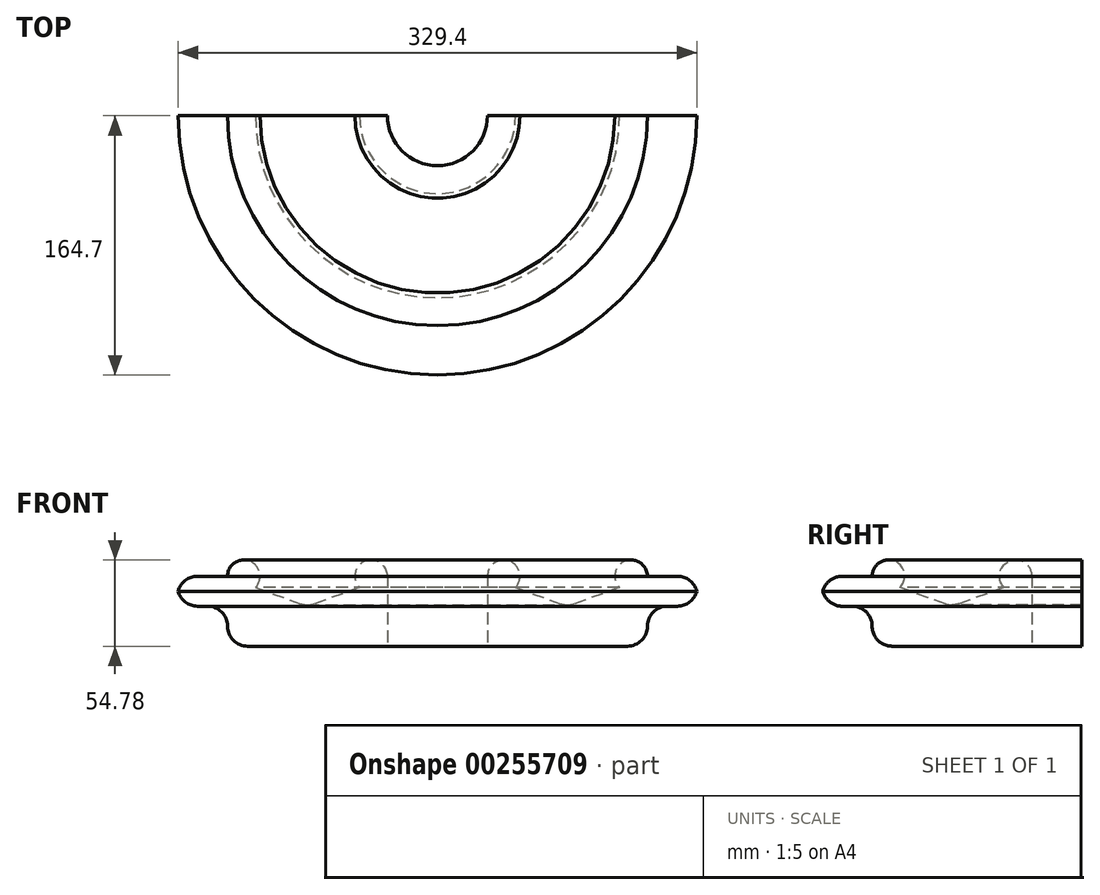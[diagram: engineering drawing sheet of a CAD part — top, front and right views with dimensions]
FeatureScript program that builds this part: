
annotation { "Feature Type Name" : "Feature", "Feature Type Description" : "" }
export const myFeature = defineFeature(function(context is Context, id is Id, definition is map)
    precondition{}
    {
        {
            var Q0;
            Q0=qCreatedBy(makeId("Front.planeOp"),FACE);
            var sketch = newSketch(context, id + "F0", { "sketchPlane" : qUnion([Q0])});
            skLineSegment(sketch, "E0.bottom", {"start": v(50.8, 12.7) * mm, "end": v(-50.8, 12.7) * mm});
            skLineSegment(sketch, "E0.top", {"start": v(50.8, -12.7) * mm, "end": v(-50.8, -12.7) * mm});
            skLineSegment(sketch, "E0.left", {"start": v(50.8, 12.7) * mm, "end": v(50.8, -12.7) * mm});
            skLineSegment(sketch, "E0.right", {"start": v(-50.8, 12.7) * mm, "end": v(-50.8, -12.7) * mm});
            skPoint(sketch, "E0.middle", {"position": v(0, 0) * mm});
            skLineSegment(sketch, "E1.bottom", {"start": v(50.8, 12.7) * mm, "end": v(82.55, 12.7) * mm});
            skLineSegment(sketch, "E1.top", {"start": v(50.8, 31.75) * mm, "end": v(82.55, 31.75) * mm});
            skLineSegment(sketch, "E1.left", {"start": v(50.8, 12.7) * mm, "end": v(50.8, 31.75) * mm});
            skLineSegment(sketch, "E1.right", {"start": v(82.55, 12.7) * mm, "end": v(82.55, 31.75) * mm});
            skLineSegment(sketch, "E2.bottom", {"start": v(-50.8, 12.7) * mm, "end": v(-82.55, 12.7) * mm});
            skLineSegment(sketch, "E2.top", {"start": v(-50.8, 31.75) * mm, "end": v(-82.55, 31.75) * mm});
            skLineSegment(sketch, "E2.left", {"start": v(-50.8, 12.7) * mm, "end": v(-50.8, 31.75) * mm});
            skLineSegment(sketch, "E2.right", {"start": v(-82.55, 12.7) * mm, "end": v(-82.55, 31.75) * mm});
            skArc(sketch, "E3", {"start": v(-33.07, 24.53) * mm, "mid": v(-36.56, 41.32) * mm, "end": v(-50.8, 31.75) * mm});
            skLineSegment(sketch, "E4", {"start": v(-33.07, 24.53) * mm, "end": v(0, 12.7) * mm});
            skArc(sketch, "E5.MirrorCS", {"start": v(33.07, 24.53) * mm, "mid": v(36.56, 41.32) * mm, "end": v(50.8, 31.75) * mm});
            skLineSegment(sketch, "E6.MirrorCS", {"start": v(33.07, 24.53) * mm, "end": v(0, 12.7) * mm});
            skSolve(sketch);
        }
        {
            var Q0;
            Q0=makeQuery(id+"F0.imprint","IMPRINT",FACE,{"disambiguationData":[TD([[makeQuery(id+"F0.imprint","IMPRINT",EDGE,{"derivedFrom":sQuery(id+"F0.wireOp",EDGE,"E2.bottom")}),-1.0]])]});
            var Q1;
            Q1=makeQuery(id+"F0.imprint","IMPRINT",FACE,{"disambiguationData":[TD([[makeQuery(id+"F0.imprint","IMPRINT",EDGE,{"derivedFrom":sQuery(id+"F0.wireOp",EDGE,"E0.top")}),-1.0]])]});
            var Q2;
            {var subQ0=sQuery(id+"F0.wireOp",EDGE,"E1.left");Q2=makeQuery(id+"F0.imprint","IMPRINT",FACE,{"disambiguationData":[TD([[makeQuery(id+"F0.imprint","IMPRINT",EDGE,{"derivedFrom":subQ0}),1.0]])]});}
            var Q3;
            {var subQ0=sQuery(id+"F0.wireOp",EDGE,"E2.left");Q3=makeQuery(id+"F0.imprint","IMPRINT",FACE,{"disambiguationData":[TD([[makeQuery(id+"F0.imprint","IMPRINT",EDGE,{"derivedFrom":subQ0}),-1.0]])]});}
            var Q4;
            Q4=sQuery(id+"F0.wireOp",EDGE,"E1.right");
            revolve(context, id + "F1", {"entities" : qUnion([Q0, Q1, Q2, Q3]), "axis" : qUnion([Q4]), "revolveType" : RevolveType.ONE_DIRECTION, "angle" : 180 * degree});
        }
        {
            var Q0;
            Q0=makeQuery(id+"F1.opRevolve","SWEPT_EDGE",EDGE,{"disambiguationData":[OSD([sQuery(id+"F0.wireOp",EDGE,"E0.bottom"),sQuery(id+"F0.wireOp",EDGE,"E4"),sQuery(id+"F0.wireOp",EDGE,"E6.MirrorCS")])]});
            fillet(context, id + "F2", {"entities" : qUnion([Q0]), "radius" : 12.7 * mm, "tangentPropagation" : true, "allowEdgeOverflow" : false});
        }
        {
            var Q0;
            Q0=makeQuery(id+"F1.opRevolve","SWEPT_EDGE",EDGE,{"disambiguationData":[OSD([sQuery(id+"F0.wireOp",EDGE,"E0.bottom"),sQuery(id+"F0.wireOp",EDGE,"E0.right"),sQuery(id+"F0.wireOp",EDGE,"E2.bottom"),sQuery(id+"F0.wireOp",EDGE,"E2.left")])]});
            fillet(context, id + "F3", {"entities" : qUnion([Q0]), "radius" : 12.7 * mm, "tangentPropagation" : true, "allowEdgeOverflow" : false});
        }
        {
            var Q0;
            Q0=makeQuery(id+"F1.opRevolve","SWEPT_EDGE",EDGE,{"disambiguationData":[OSD([sQuery(id+"F0.wireOp",EDGE,"E2.top"),sQuery(id+"F0.wireOp",EDGE,"E2.right")])]});
            var Q1;
            Q1=makeQuery(id+"F1.opRevolve","SWEPT_EDGE",EDGE,{"disambiguationData":[OSD([sQuery(id+"F0.wireOp",EDGE,"E2.bottom"),sQuery(id+"F0.wireOp",EDGE,"E2.right")])]});
            var Q2;
            Q2=makeQuery(id+"F1.opRevolve","SWEPT_EDGE",EDGE,{"disambiguationData":[OSD([sQuery(id+"F0.wireOp",EDGE,"E0.top"),sQuery(id+"F0.wireOp",EDGE,"E0.right")])]});
            fillet(context, id + "F4", {"entities" : qUnion([Q0, Q1, Q2]), "radius" : 12.7 * mm, "tangentPropagation" : true, "allowEdgeOverflow" : false});
        }
    });
